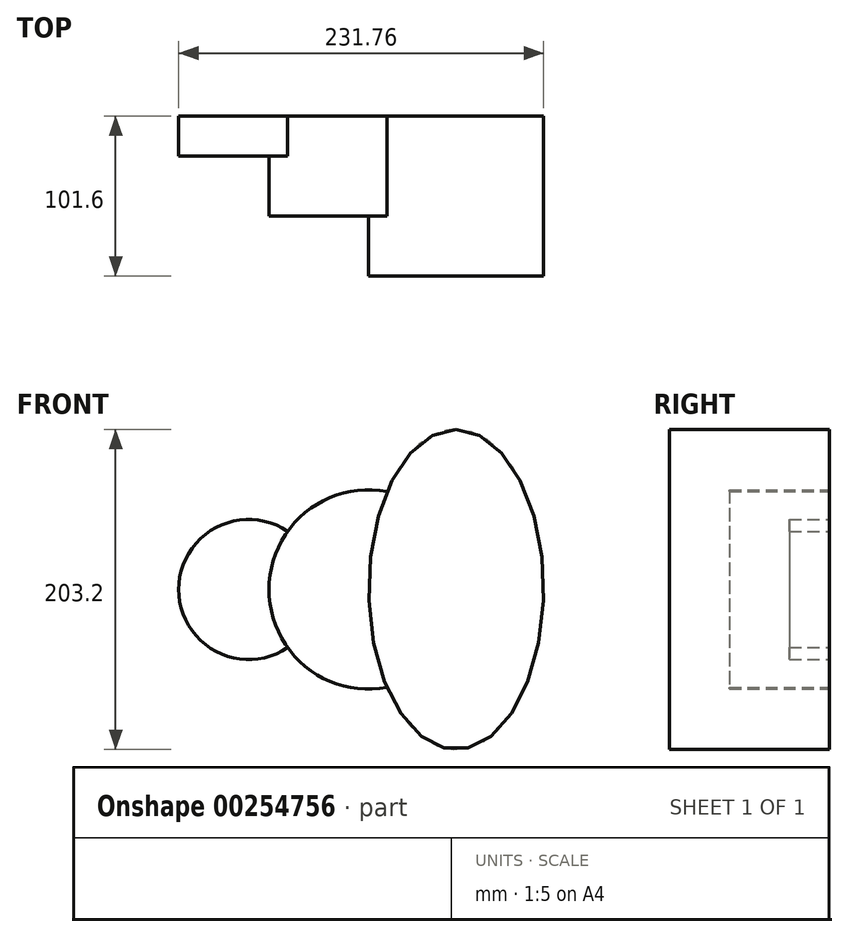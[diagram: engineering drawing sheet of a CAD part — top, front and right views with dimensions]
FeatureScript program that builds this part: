
annotation { "Feature Type Name" : "Feature", "Feature Type Description" : "" }
export const myFeature = defineFeature(function(context is Context, id is Id, definition is map)
    precondition{}
    {
        {
            var Q0;
            Q0=qCreatedBy(makeId("Front.planeOp"),FACE);
            var sketch = newSketch(context, id + "F0", { "sketchPlane" : qUnion([Q0])});
            skCircle(sketch, "E0", {"center": v(0, 0) * mm, "radius": 63.3 * mm});
            skSolve(sketch);
        }
        {
            var Q0;
            Q0=qCreatedBy(makeId("Front.planeOp"),FACE);
            var sketch = newSketch(context, id + "F1", { "sketchPlane" : qUnion([Q0])});
            skLineSegment(sketch, "E1", {"start": v(0, 0) * mm, "end": v(-76.2, 0) * mm});
            skCircle(sketch, "E2", {"center": v(-76.2, 0) * mm, "radius": 44.45 * mm});
            skSolve(sketch);
        }
        {
            var Q0;
            Q0=qCreatedBy(makeId("Front.planeOp"),FACE);
            var sketch = newSketch(context, id + "F2", { "sketchPlane" : qUnion([Q0])});
            skLineSegment(sketch, "E3", {"start": v(0, 0) * mm, "end": v(55.55, 0) * mm});
            skLineSegment(sketch, "E4", {"start": v(55.55, 0) * mm, "end": v(55.55, 101.6) * mm});
            skEllipse(sketch, "E5", {"center": v(55.55, 0) * mm, "majorRadius": 101.6 * mm, "minorRadius": 55.55 * mm, "majorAxis": v(0, 1)});
            skSolve(sketch);
        }
        {
            var Q0;
            Q0=qCreatedBy(makeId("Front.planeOp"),FACE);
            var sketch = newSketch(context, id + "F3", { "sketchPlane" : qUnion([Q0])});
            skSolve(sketch);
        }
        {
            var Q0;
            Q0 = qSketchRegion(id + "F3", true);
            var Q1;
            Q1=makeQuery(id+"F1.imprint","IMPRINT",FACE,{"disambiguationData":[TD([[makeQuery(id+"F1.imprint","IMPRINT",EDGE,{"derivedFrom":sQuery(id+"F1.wireOp",EDGE,"E2")}),1.0]])]});
            extrude(context, id + "F4", {"entities" : qUnion([Q0, Q1]), "depth" : 25.4 * mm});
        }
        {
            var Q0;
            Q0=makeQuery(id+"F0.imprint","IMPRINT",FACE,{"disambiguationData":[TD([[makeQuery(id+"F0.imprint","IMPRINT",EDGE,{"derivedFrom":sQuery(id+"F0.wireOp",EDGE,"E0")}),1.0]])]});
            extrude(context, id + "F5", {"entities" : qUnion([Q0]), "operationType" : NewBodyOperationType.ADD, "depth" : 63.5 * mm});
        }
        {
            var Q0;
            {var subQ0=sQuery(id+"F2.wireOp",EDGE,"E3");Q0=makeQuery(id+"F2.imprint","IMPRINT",FACE,{"disambiguationData":[TD([[makeQuery(id+"F2.imprint","IMPRINT",EDGE,{"derivedFrom":subQ0}),-1.0]])]});}
            var Q1;
            {var subQ0=sQuery(id+"F2.wireOp",EDGE,"E3");Q1=makeQuery(id+"F2.imprint","IMPRINT",FACE,{"disambiguationData":[TD([[makeQuery(id+"F2.imprint","IMPRINT",EDGE,{"derivedFrom":subQ0}),1.0]])]});}
            extrude(context, id + "F6", {"entities" : qUnion([Q0, Q1]), "operationType" : NewBodyOperationType.ADD, "depth" : 101.6 * mm});
        }
    });
